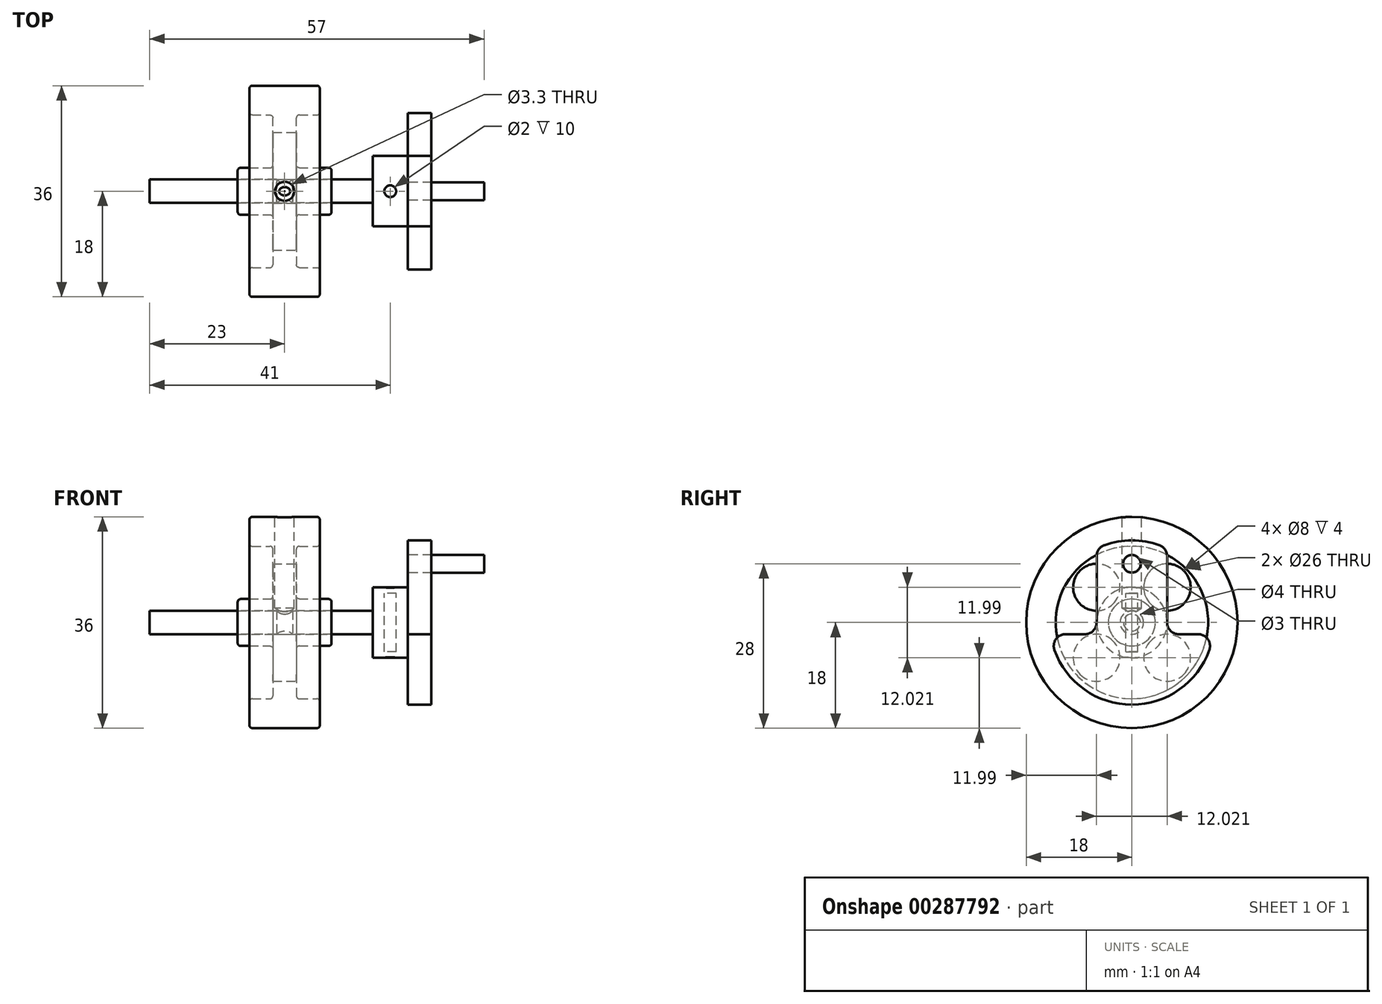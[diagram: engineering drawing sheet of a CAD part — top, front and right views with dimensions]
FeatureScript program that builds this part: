
annotation { "Feature Type Name" : "Feature", "Feature Type Description" : "" }
export const myFeature = defineFeature(function(context is Context, id is Id, definition is map)
    precondition{}
    {
        {
            var Q0;
            Q0=qCreatedBy(makeId("Front.planeOp"),FACE);
            var sketch = newSketch(context, id + "F0", { "sketchPlane" : qUnion([Q0])});
            skLineSegment(sketch, "E0.top", {"start": v(-23, 28) * mm, "end": v(-1.38, 28) * mm});
            skLineSegment(sketch, "E0.right", {"start": v(25, 26) * mm, "end": v(25, 28) * mm});
            skArc(sketch, "E1", {"start": v(1.38, 28) * mm, "mid": v(0, 27.44) * mm, "end": v(-1.38, 28) * mm});
            skLineSegment(sketch, "E2.trimOffspring", {"start": v(1.38, 28) * mm, "end": v(25, 28) * mm});
            skLineSegment(sketch, "E3", {"start": v(-23, 26) * mm, "end": v(25, 26) * mm});
            skLineSegment(sketch, "E4", {"start": v(-23, 28) * mm, "end": v(-23, 26) * mm});
            skSolve(sketch);
        }
        {
            var Q0;
            Q0=makeQuery(id+"F0.imprint","IMPRINT",FACE,{"disambiguationData":[TD([[makeQuery(id+"F0.imprint","IMPRINT",EDGE,{"derivedFrom":sQuery(id+"F0.wireOp",EDGE,"E0.top")}),-1.0]])]});
            var Q1;
            Q1=sQuery(id+"F0.wireOp",EDGE,"E3");
            revolve(context, id + "F1", {"entities" : qUnion([Q0]), "axis" : qUnion([Q1]), "revolveType" : RevolveType.FULL});
        }
        {
            var Q0;
            Q0=qCreatedBy(makeId("Front.planeOp"),FACE);
            var sketch = newSketch(context, id + "F2", { "sketchPlane" : qUnion([Q0])});
            skLineSegment(sketch, "E5", {"start": v(8, 22) * mm, "end": v(2, 22) * mm});
            skLineSegment(sketch, "E6", {"start": v(2, 22) * mm, "end": v(2, 13) * mm});
            skLineSegment(sketch, "E7", {"start": v(2, 13) * mm, "end": v(6, 13) * mm});
            skLineSegment(sketch, "E8", {"start": v(6, 13) * mm, "end": v(6, 8) * mm});
            skLineSegment(sketch, "E9", {"start": v(6, 8) * mm, "end": v(-6, 8) * mm});
            skLineSegment(sketch, "E10", {"start": v(-6, 8) * mm, "end": v(-6, 13) * mm});
            skLineSegment(sketch, "E11", {"start": v(-6, 13) * mm, "end": v(-2, 13) * mm});
            skLineSegment(sketch, "E12", {"start": v(-2, 13) * mm, "end": v(-2, 22) * mm});
            skLineSegment(sketch, "E13", {"start": v(-2, 22) * mm, "end": v(-8, 22) * mm});
            skLineSegment(sketch, "E14", {"start": v(0, 13) * mm, "end": v(0, -15.49) * mm, "construction": true});
            skLineSegment(sketch, "E15", {"start": v(-8, 24) * mm, "end": v(8, 24) * mm});
            skLineSegment(sketch, "E16", {"start": v(-8, 24) * mm, "end": v(-8, 22) * mm});
            skLineSegment(sketch, "E17", {"start": v(8, 24) * mm, "end": v(8, 22) * mm});
            skLineSegment(sketch, "E18", {"start": v(16, 26) * mm, "end": v(-3.74, 26) * mm, "construction": true});
            skSolve(sketch);
        }
        {
            var Q0;
            Q0 = qSketchRegion(id + "F2", true);
            var Q1;
            Q1=sQuery(id+"F2.wireOp",EDGE,"E18");
            revolve(context, id + "F3", {"entities" : qUnion([Q0]), "axis" : qUnion([Q1]), "revolveType" : RevolveType.FULL});
        }
        {
            var Q0;
            Q0=makeQuery(id+"F3.opRevolve","SWEPT_FACE",FACE,{"disambiguationData":[OSD([sQuery(id+"F2.wireOp",EDGE,"E6")])]});
            var sketch = newSketch(context, id + "F4", { "sketchPlane" : qUnion([Q0])});
            skCircle(sketch, "E19", {"center": v(0, 26) * mm, "radius": 8.5 * mm, "construction": true});
            skLineSegment(sketch, "E20", {"start": v(0, 3.94) * mm, "end": v(0, 47.32) * mm, "construction": true});
            skLineSegment(sketch, "E21", {"start": v(-22.8, 26) * mm, "end": v(26.66, 26) * mm, "construction": true});
            skLineSegment(sketch, "E22", {"start": v(0, 26) * mm, "end": v(17.86, 8.14) * mm, "construction": true});
            skLineSegment(sketch, "E23", {"start": v(0, 26) * mm, "end": v(-17.18, 8.82) * mm, "construction": true});
            skLineSegment(sketch, "E24", {"start": v(0, 26) * mm, "end": v(-16.24, 42.24) * mm, "construction": true});
            skLineSegment(sketch, "E25", {"start": v(0, 26) * mm, "end": v(20.02, 46.02) * mm, "construction": true});
            skCircle(sketch, "E26", {"center": v(-6.01, 32.01) * mm, "radius": 4 * mm});
            skCircle(sketch, "E27", {"center": v(6.01, 32.01) * mm, "radius": 4 * mm});
            skCircle(sketch, "E28", {"center": v(6.01, 19.99) * mm, "radius": 4 * mm});
            skCircle(sketch, "E29", {"center": v(-6.01, 19.99) * mm, "radius": 4 * mm});
            skSolve(sketch);
        }
        {
            var Q0;
            Q0 = qSketchRegion(id + "F4", true);
            extrude(context, id + "F5", {"entities" : qUnion([Q0]), "operationType" : NewBodyOperationType.REMOVE, "endBound" : BoundingType.THROUGH_ALL, "oppositeDirection" : true, "depth" : 25 * mm});
        }
        {
            var Q0;
            Q0=makeQuery(id+"F3.opRevolve","SWEPT_EDGE",EDGE,{"disambiguationData":[OSD([sQuery(id+"F2.wireOp",EDGE,"E8"),sQuery(id+"F2.wireOp",EDGE,"E9")])]});
            var Q1;
            Q1=makeQuery(id+"F3.opRevolve","SWEPT_EDGE",EDGE,{"disambiguationData":[OSD([sQuery(id+"F2.wireOp",EDGE,"E9"),sQuery(id+"F2.wireOp",EDGE,"E10")])]});
            var Q2;
            Q2=makeQuery(id+"F3.opRevolve","SWEPT_EDGE",EDGE,{"disambiguationData":[OSD([sQuery(id+"F2.wireOp",EDGE,"E7"),sQuery(id+"F2.wireOp",EDGE,"E8")])]});
            var Q3;
            Q3=makeQuery(id+"F3.opRevolve","SWEPT_EDGE",EDGE,{"disambiguationData":[OSD([sQuery(id+"F2.wireOp",EDGE,"E10"),sQuery(id+"F2.wireOp",EDGE,"E11")])]});
            var Q4;
            Q4=makeQuery(id+"F3.opRevolve","SWEPT_EDGE",EDGE,{"disambiguationData":[OSD([sQuery(id+"F2.wireOp",EDGE,"E11"),sQuery(id+"F2.wireOp",EDGE,"E12")])]});
            var Q5;
            Q5=makeQuery(id+"F3.opRevolve","SWEPT_EDGE",EDGE,{"disambiguationData":[OSD([sQuery(id+"F2.wireOp",EDGE,"E6"),sQuery(id+"F2.wireOp",EDGE,"E7")])]});
            var Q6;
            Q6=makeQuery(id+"F3.opRevolve","SWEPT_EDGE",EDGE,{"disambiguationData":[OSD([sQuery(id+"F2.wireOp",EDGE,"E5"),sQuery(id+"F2.wireOp",EDGE,"E17")])]});
            var Q7;
            Q7=makeQuery(id+"F3.opRevolve","SWEPT_EDGE",EDGE,{"disambiguationData":[OSD([sQuery(id+"F2.wireOp",EDGE,"E5"),sQuery(id+"F2.wireOp",EDGE,"E6")])]});
            var Q8;
            Q8=makeQuery(id+"F3.opRevolve","SWEPT_EDGE",EDGE,{"disambiguationData":[OSD([sQuery(id+"F2.wireOp",EDGE,"E13"),sQuery(id+"F2.wireOp",EDGE,"E16")])]});
            var Q9;
            Q9=makeQuery(id+"F3.opRevolve","SWEPT_EDGE",EDGE,{"disambiguationData":[OSD([sQuery(id+"F2.wireOp",EDGE,"E12"),sQuery(id+"F2.wireOp",EDGE,"E13")])]});
            fillet(context, id + "F6", {"entities" : qUnion([Q0, Q1, Q2, Q3, Q4, Q5, Q6, Q7, Q8, Q9]), "radius" : 0.5 * mm, "tangentPropagation" : true, "allowEdgeOverflow" : false});
        }
        {
            var Q0;
            Q0=qCreatedBy(makeId("Top.planeOp"),FACE);
            cPlane(context, id + "F7", {"entities" : qUnion([Q0]), "cplaneType" : CPlaneType.OFFSET, "offset" : 26 * mm, "width" : 150 * mm, "height" : 150 * mm});
        }
        {
            var Q0;
            Q0=qCreatedBy(id+"F7.planeOp",FACE);
            var sketch = newSketch(context, id + "F8", { "sketchPlane" : qUnion([Q0])});
            skCircle(sketch, "E30", {"center": v(18, 0) * mm, "radius": 1 * mm});
            skSolve(sketch);
        }
        {
            var Q0;
            Q0 = qSketchRegion(id + "F8", true);
            extrude(context, id + "F9", {"entities" : qUnion([Q0]), "operationType" : NewBodyOperationType.REMOVE, "endBound" : BoundingType.SYMMETRIC, "oppositeDirection" : true, "depth" : 10 * mm});
        }
        {
            var Q0;
            Q0 = qSketchRegion(id + "F8", true);
            extrude(context, id + "F10", {"entities" : qUnion([Q0]), "endBound" : BoundingType.SYMMETRIC, "depth" : 12 * mm});
        }
        {
            var Q0;
            Q0=makeQuery(id+"F3.opRevolve","SWEPT_FACE",FACE,{"disambiguationData":[OSD([sQuery(id+"F2.wireOp",EDGE,"E17")])]});
            cPlane(context, id + "F11", {"entities" : qUnion([Q0]), "cplaneType" : CPlaneType.OFFSET, "offset" : 13 * mm, "width" : 150 * mm, "height" : 150 * mm});
        }
        {
            var Q0;
            Q0=qCreatedBy(id+"F11.planeOp",FACE);
            var sketch = newSketch(context, id + "F12", { "sketchPlane" : qUnion([Q0])});
            skArc(sketch, "E31", {"start": v(-13.2, 21.33) * mm, "mid": v(0, 12) * mm, "end": v(13.2, 21.33) * mm});
            skLineSegment(sketch, "E32", {"start": v(0, 44.32) * mm, "end": v(0, 9) * mm, "construction": true});
            skLineSegment(sketch, "E33", {"start": v(20.3, 26) * mm, "end": v(-23.7, 26) * mm, "construction": true});
            skLineSegment(sketch, "E34", {"start": v(-11.31, 24) * mm, "end": v(-8, 24) * mm});
            skLineSegment(sketch, "E35", {"start": v(-6, 26) * mm, "end": v(-6, 37.31) * mm});
            skLineSegment(sketch, "E36", {"start": v(11.31, 24) * mm, "end": v(8, 24) * mm});
            skLineSegment(sketch, "E37", {"start": v(6, 26) * mm, "end": v(6, 37.31) * mm});
            skArc(sketch, "E38.trimOffspring", {"start": v(4.67, 39.2) * mm, "mid": v(0, 40) * mm, "end": v(-4.67, 39.2) * mm});
            skPoint(sketch, "E39.visualSharp", {"position": v(6, 24) * mm});
            skArc(sketch, "E39.filletArc", {"start": v(6, 26) * mm, "mid": v(6.59, 24.59) * mm, "end": v(8, 24) * mm});
            skPoint(sketch, "E40.visualSharp", {"position": v(-6, 24) * mm});
            skArc(sketch, "E40.filletArc", {"start": v(-8, 24) * mm, "mid": v(-6.59, 24.59) * mm, "end": v(-6, 26) * mm});
            skPoint(sketch, "E41.visualSharp", {"position": v(13.86, 24) * mm});
            skArc(sketch, "E41.filletArc", {"start": v(13.2, 21.33) * mm, "mid": v(12.95, 23.15) * mm, "end": v(11.31, 24) * mm});
            skPoint(sketch, "E42.visualSharp", {"position": v(-13.86, 24) * mm});
            skArc(sketch, "E42.filletArc", {"start": v(-11.31, 24) * mm, "mid": v(-12.95, 23.15) * mm, "end": v(-13.2, 21.33) * mm});
            skPoint(sketch, "E43.visualSharp", {"position": v(-6, 38.65) * mm});
            skArc(sketch, "E43.filletArc", {"start": v(-4.67, 39.2) * mm, "mid": v(-5.63, 38.47) * mm, "end": v(-6, 37.31) * mm});
            skPoint(sketch, "E44.visualSharp", {"position": v(6, 38.65) * mm});
            skArc(sketch, "E44.filletArc", {"start": v(6, 37.31) * mm, "mid": v(5.63, 38.47) * mm, "end": v(4.67, 39.2) * mm});
            skCircle(sketch, "E45", {"center": v(0, 36) * mm, "radius": 1.5 * mm});
            skCircle(sketch, "E46", {"center": v(0, 26) * mm, "radius": 2 * mm});
            skSolve(sketch);
        }
        {
            var Q0;
            Q0 = qSketchRegion(id + "F12", true);
            extrude(context, id + "F13", {"entities" : qUnion([Q0]), "depth" : 4 * mm});
        }
        {
            var Q0;
            Q0=makeQuery(id+"F13.opExtrude","CAP_FACE",FACE,{"disambiguationData":[OSD([sQuery(id+"F12.wireOp",EDGE,"E31"),sQuery(id+"F12.wireOp",EDGE,"E34"),sQuery(id+"F12.wireOp",EDGE,"E35"),sQuery(id+"F12.wireOp",EDGE,"E36"),sQuery(id+"F12.wireOp",EDGE,"E37"),sQuery(id+"F12.wireOp",EDGE,"E38.trimOffspring"),sQuery(id+"F12.wireOp",EDGE,"E39.filletArc"),sQuery(id+"F12.wireOp",EDGE,"E40.filletArc"),sQuery(id+"F12.wireOp",EDGE,"E41.filletArc"),sQuery(id+"F12.wireOp",EDGE,"E42.filletArc"),sQuery(id+"F12.wireOp",EDGE,"E43.filletArc"),sQuery(id+"F12.wireOp",EDGE,"E44.filletArc"),sQuery(id+"F12.wireOp",EDGE,"E45"),sQuery(id+"F12.wireOp",EDGE,"E46")])],"isStart":true});
            var sketch = newSketch(context, id + "F14", { "sketchPlane" : qUnion([Q0])});
            skCircle(sketch, "E47", {"center": v(0, 26) * mm, "radius": 6 * mm});
            skCircle(sketch, "E48", {"center": v(0, 26) * mm, "radius": 2 * mm});
            skSolve(sketch);
        }
        {
            var Q0;
            Q0 = qSketchRegion(id + "F14", true);
            extrude(context, id + "F15", {"entities" : qUnion([Q0]), "operationType" : NewBodyOperationType.ADD, "depth" : 6 * mm});
        }
        {
            var Q0;
            Q0 = qSketchRegion(id + "F8", true);
            extrude(context, id + "F16", {"entities" : qUnion([Q0]), "operationType" : NewBodyOperationType.REMOVE, "endBound" : BoundingType.SYMMETRIC, "oppositeDirection" : true, "depth" : 10 * mm});
        }
        {
            var Q0;
            Q0=makeQuery(id+"F12.imprint","IMPRINT",FACE,{"disambiguationData":[TD([[makeQuery(id+"F12.imprint","IMPRINT",EDGE,{"derivedFrom":sQuery(id+"F12.wireOp",EDGE,"E45")}),1.0]])]});
            extrude(context, id + "F17", {"entities" : qUnion([Q0]), "depth" : 13 * mm});
        }
        {
            var Q0;
            Q0=qCreatedBy(makeId("Top.planeOp"),FACE);
            cPlane(context, id + "F18", {"entities" : qUnion([Q0]), "cplaneType" : CPlaneType.OFFSET, "offset" : 44 * mm, "width" : 150 * mm, "height" : 150 * mm});
        }
        {
            var Q0;
            Q0=qCreatedBy(id+"F18.planeOp",FACE);
            var sketch = newSketch(context, id + "F19", { "sketchPlane" : qUnion([Q0])});
            skPoint(sketch, "E49", {"position": v(0, 0) * mm});
            skSolve(sketch);
        }
        {
            var Q0;
            Q0=sQuery(id+"F19.wireOp",VERTEX,"E49");
            var Q1;
            Q1=makeQuery(id+"F3.opRevolve","SWEPT_BODY",BODY,{"disambiguationData":[OSD([sQuery(id+"F2.wireOp",EDGE,"E5"),sQuery(id+"F2.wireOp",EDGE,"E6"),sQuery(id+"F2.wireOp",EDGE,"E7"),sQuery(id+"F2.wireOp",EDGE,"E8"),sQuery(id+"F2.wireOp",EDGE,"E9"),sQuery(id+"F2.wireOp",EDGE,"E10"),sQuery(id+"F2.wireOp",EDGE,"E11"),sQuery(id+"F2.wireOp",EDGE,"E12"),sQuery(id+"F2.wireOp",EDGE,"E13"),sQuery(id+"F2.wireOp",EDGE,"E15"),sQuery(id+"F2.wireOp",EDGE,"E16"),sQuery(id+"F2.wireOp",EDGE,"E17")])]});
            var Q2;
            Q2=makeQuery(id+"F1.opRevolve","SWEPT_BODY",BODY,{"disambiguationData":[OSD([sQuery(id+"F0.wireOp",EDGE,"E0.top"),sQuery(id+"F0.wireOp",EDGE,"E0.right"),sQuery(id+"F0.wireOp",EDGE,"E1"),sQuery(id+"F0.wireOp",EDGE,"E2.trimOffspring"),sQuery(id+"F0.wireOp",EDGE,"E3"),sQuery(id+"F0.wireOp",EDGE,"E4")])]});
            hole(context, id + "F20", {"style" : HoleStyle.SIMPLE, "endStyle" : HoleEndStyle.BLIND, "standardTappedOrClearance" : lookupTablePath({ "standard" : "ISO", "fit" : "Normal", "size" : "M3", "type" : "Clearance" }), "standardBlindInLast" : lookupTablePath({ "fit" : "Standard", "standard" : "ISO", "size" : "M3", "type" : "Clearance" }), "holeDiameter" : 3.3 * mm, "holeDepth" : 15.5 * mm, "tappedDepth" : 3 * mm, "tapClearance" : 3, "locations" : qUnion([Q0]), "scope" : qUnion([Q1, Q2])});
        }
    });
